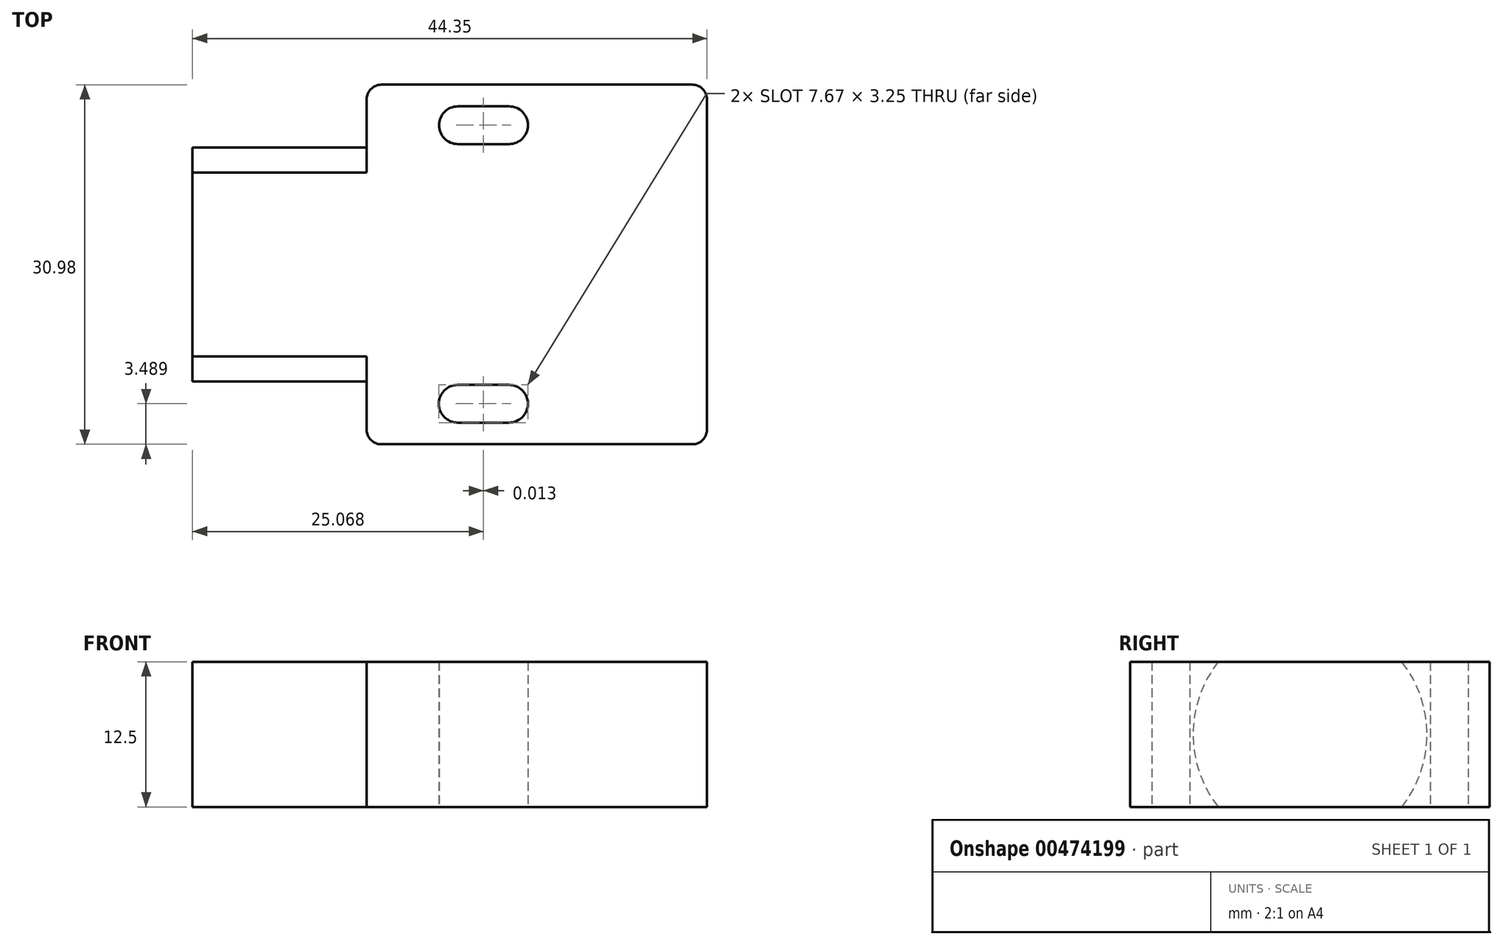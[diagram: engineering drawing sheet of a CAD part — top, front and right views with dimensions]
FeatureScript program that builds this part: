
annotation { "Feature Type Name" : "Feature", "Feature Type Description" : "" }
export const myFeature = defineFeature(function(context is Context, id is Id, definition is map)
    precondition{}
    {
        {
            var Q0;
            Q0=qCreatedBy(makeId("Top.planeOp"),FACE);
            var sketch = newSketch(context, id + "F0", { "sketchPlane" : qUnion([Q0])});
            skLineSegment(sketch, "E0", {"start": v(25.88, 15.5) * mm, "end": v(25.88, -15.5) * mm});
            skLineSegment(sketch, "E1", {"start": v(25.88, -15.5) * mm, "end": v(-3.46, -15.5) * mm});
            skLineSegment(sketch, "E2", {"start": v(-3.46, -15.5) * mm, "end": v(-3.46, -10.08) * mm});
            skLineSegment(sketch, "E3", {"start": v(-3.46, -10.08) * mm, "end": v(-18.47, -10.08) * mm});
            skLineSegment(sketch, "E4", {"start": v(-18.47, -10.08) * mm, "end": v(-18.47, 10.08) * mm});
            skLineSegment(sketch, "E5", {"start": v(-18.47, 10.08) * mm, "end": v(-3.46, 10.08) * mm});
            skLineSegment(sketch, "E6", {"start": v(-3.46, 10.08) * mm, "end": v(-3.46, 15.5) * mm});
            skLineSegment(sketch, "E7", {"start": v(-3.46, 15.5) * mm, "end": v(25.88, 15.5) * mm});
            skLineSegment(sketch, "E8", {"start": v(-18.07, 0) * mm, "end": v(0, 0) * mm});
            skPoint(sketch, "E8.startSnap0", {"position": v(-18.47, 0) * mm});
            skLineSegment(sketch, "E9", {"start": v(4.4, 13.63) * mm, "end": v(8.82, 13.63) * mm});
            skLineSegment(sketch, "E10", {"start": v(4.4, 10.38) * mm, "end": v(8.82, 10.38) * mm});
            skArc(sketch, "E11", {"start": v(4.4, 13.63) * mm, "mid": v(2.78, 12) * mm, "end": v(4.4, 10.38) * mm});
            skArc(sketch, "E12", {"start": v(8.82, 13.63) * mm, "mid": v(10.45, 12) * mm, "end": v(8.82, 10.38) * mm});
            skLineSegment(sketch, "E13", {"start": v(4.39, -10.38) * mm, "end": v(8.8, -10.38) * mm});
            skLineSegment(sketch, "E14", {"start": v(4.39, -13.63) * mm, "end": v(8.8, -13.63) * mm});
            skArc(sketch, "E15", {"start": v(4.39, -10.38) * mm, "mid": v(2.76, -12) * mm, "end": v(4.39, -13.63) * mm});
            skArc(sketch, "E16", {"start": v(8.8, -10.38) * mm, "mid": v(10.43, -12) * mm, "end": v(8.8, -13.63) * mm});
            skSolve(sketch);
        }
        {
            var Q0;
            Q0=makeQuery(id+"F0.imprint","IMPRINT",FACE,{"disambiguationData":[TD([[makeQuery(id+"F0.imprint","IMPRINT",EDGE,{"derivedFrom":sQuery(id+"F0.wireOp",EDGE,"E0")}),-1.0]])]});
            extrude(context, id + "F1", {"entities" : qUnion([Q0]), "depth" : 12.5 * mm, "offsetDistance" : 25.4 * mm});
        }
        {
            var Q0;
            Q0=makeQuery(id+"F1.opExtrude","SWEPT_FACE",FACE,{"disambiguationData":[OSD([sQuery(id+"F0.wireOp",EDGE,"E4")])]});
            var sketch = newSketch(context, id + "F2", { "sketchPlane" : qUnion([Q0])});
            skPoint(sketch, "E17.centerSnap0", {"position": v(10.08, 6.25) * mm});
            skCircle(sketch, "E18", {"center": v(0, 6.25) * mm, "radius": 10.08 * mm});
            skSolve(sketch);
        }
        {
            var Q0;
            Q0=makeQuery(id+"F1.opExtrude","SWEPT_EDGE",EDGE,{"disambiguationData":[OSD([sQuery(id+"F0.wireOp",EDGE,"E1"),sQuery(id+"F0.wireOp",EDGE,"E2")])]});
            var Q1;
            Q1=makeQuery(id+"F1.opExtrude","SWEPT_EDGE",EDGE,{"disambiguationData":[OSD([sQuery(id+"F0.wireOp",EDGE,"E6"),sQuery(id+"F0.wireOp",EDGE,"E7")])]});
            var Q2;
            Q2=makeQuery(id+"F1.opExtrude","SWEPT_EDGE",EDGE,{"disambiguationData":[OSD([sQuery(id+"F0.wireOp",EDGE,"E0"),sQuery(id+"F0.wireOp",EDGE,"E1")])]});
            var Q3;
            Q3=makeQuery(id+"F1.opExtrude","SWEPT_EDGE",EDGE,{"disambiguationData":[OSD([sQuery(id+"F0.wireOp",EDGE,"E0"),sQuery(id+"F0.wireOp",EDGE,"E7")])]});
            fillet(context, id + "F3", {"entities" : qUnion([Q0, Q1, Q2, Q3]), "radius" : 1.27 * mm, "tangentPropagation" : true, "allowEdgeOverflow" : false});
        }
        {
            var Q0;
            {var subQ0=sQuery(id+"F2.wireOp",EDGE,"E18");var subQ1=sQuery(id+"F0.wireOp",EDGE,"E4");var subQ2=makeQuery(id+"F1.opExtrude","CAP_EDGE",EDGE,{"disambiguationData":[OSD([subQ1])],"isStart":false});var subQ3=makeQuery(id+"F2.imprint","INTERSECT",VERTEX,{"disambiguationData":[OD(1.0)],"derivedFrom":[subQ2,subQ0]});Q0=makeQuery(id+"F2.imprint","IMPRINT",FACE,{"disambiguationData":[TD([[makeQuery(id+"F2.imprint","IMPRINT",EDGE,{"disambiguationData":[TD([[subQ3,-1.0]])],"derivedFrom":subQ0}),-1.0]])]});}
            var Q1;
            {var subQ0=sQuery(id+"F2.wireOp",EDGE,"E18");var subQ1=sQuery(id+"F0.wireOp",EDGE,"E4");var subQ4=makeQuery(id+"F1.opExtrude","CAP_EDGE",EDGE,{"disambiguationData":[OSD([subQ1])],"isStart":true});var subQ5=makeQuery(id+"F2.imprint","INTERSECT",VERTEX,{"disambiguationData":[OD(0.0)],"derivedFrom":[subQ4,subQ0]});Q1=makeQuery(id+"F2.imprint","IMPRINT",FACE,{"disambiguationData":[TD([[makeQuery(id+"F2.imprint","IMPRINT",EDGE,{"disambiguationData":[TD([[subQ5,1.0]])],"derivedFrom":subQ0}),-1.0]])]});}
            var Q2;
            {var subQ0=sQuery(id+"F2.wireOp",EDGE,"E18");var subQ1=sQuery(id+"F0.wireOp",EDGE,"E4");var subQ4=makeQuery(id+"F1.opExtrude","CAP_EDGE",EDGE,{"disambiguationData":[OSD([subQ1])],"isStart":true});var subQ5=makeQuery(id+"F2.imprint","INTERSECT",VERTEX,{"disambiguationData":[OD(1.0)],"derivedFrom":[subQ4,subQ0]});Q2=makeQuery(id+"F2.imprint","IMPRINT",FACE,{"disambiguationData":[TD([[makeQuery(id+"F2.imprint","IMPRINT",EDGE,{"disambiguationData":[TD([[subQ5,-1.0]])],"derivedFrom":subQ0}),-1.0]])]});}
            var Q3;
            {var subQ0=sQuery(id+"F2.wireOp",EDGE,"E18");var subQ1=sQuery(id+"F0.wireOp",EDGE,"E4");var subQ2=makeQuery(id+"F1.opExtrude","CAP_EDGE",EDGE,{"disambiguationData":[OSD([subQ1])],"isStart":false});var subQ3=makeQuery(id+"F2.imprint","INTERSECT",VERTEX,{"disambiguationData":[OD(0.0)],"derivedFrom":[subQ2,subQ0]});Q3=makeQuery(id+"F2.imprint","IMPRINT",FACE,{"disambiguationData":[TD([[makeQuery(id+"F2.imprint","IMPRINT",EDGE,{"disambiguationData":[TD([[subQ3,1.0]])],"derivedFrom":subQ0}),-1.0]])]});}
            extrude(context, id + "F4", {"entities" : qUnion([Q0, Q1, Q2, Q3]), "operationType" : NewBodyOperationType.REMOVE, "oppositeDirection" : true, "depth" : 15 * mm, "offsetDistance" : 25.4 * mm});
        }
    });
